FCSTD DOCUMENT
Label: Wheel
objects: Sketcher::SketchObject×1
note: 1 computed .brp shape members not serialized (recipe doc carries the construction recipe); baked Part::Feature solids carry a one-line shape summary decoded from their .brp

FEATURE [Sketcher::SketchObject] Sketch
  Placement = pos=(0,0,0) rot=(1,0,0;1.5708rad)
  sketch-geometry (8):
    g0: LineSegment StartX=0 StartY=1.67432 StartZ=0 EndX=1.45 EndY=0.837157 EndZ=0
    g1: LineSegment StartX=1.45 StartY=-0.837159 StartZ=0 EndX=-1.93528e-06 EndY=-1.67432 EndZ=0
    g2: LineSegment StartX=-1.93528e-06 StartY=-1.67432 StartZ=0 EndX=-1.45 EndY=-0.837157 EndZ=0
    g3: LineSegment StartX=-1.45 StartY=-0.837157 StartZ=0 EndX=-1.45 EndY=0.837158 EndZ=0
    g4: LineSegment StartX=-1.45 StartY=0.837158 StartZ=0 EndX=0 EndY=1.67432 EndZ=0
    g5: LineSegment StartX=1.45 StartY=-0.837159 StartZ=0 EndX=1.45 EndY=0.837157 EndZ=0
    g6: LineSegment StartX=0 StartY=1.67432 StartZ=0 EndX=0 EndY=0 EndZ=0
    g7: Circle CenterX=0 CenterY=0 CenterZ=0 NormalX=0 NormalY=0 NormalZ=1 Radius=30
  constraints (14):
    c: Coincident(g1,g2)
    c: Coincident(g2,g3)
    c: Coincident(g3,g4)
    c: Coincident(g4,g0)
    c: Coincident(g5,g1)
    c: Coincident(g5,g0)
    c: Angle(g2,g3) = 2.0944
    c: Angle(g0,g5) = 2.0944
    c: Angle(g4,g0) = 2.0944
    c: Distance(g0,g2) = 2.9
    c: Coincident(g6,g0)
    c: Coincident(g6,g-1)
    c: Coincident(g7,g-1)
    c: Radius(g7) = 30
